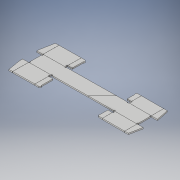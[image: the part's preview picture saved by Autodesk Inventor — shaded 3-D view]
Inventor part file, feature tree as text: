
AUTODESK INVENTOR PART (.ipt)
format: ipt  version: 2019 (Build 230136000, 136)  size: 731,648 bytes
history: native  units: mm
features: sheet_metal_op x10, sketch x4, projected_geometry x3, other x2
ambient origin geometry x8: Origin, YZ Plane, XZ Plane, XY Plane, X Axis, Y Axis, Z Axis, Center Point
bodies: Solid1 (feature_tree)
feature tree (19):
  sheet_metal_op  "Face1"
  sketch  "Sketch3"  dims[d13=5.0mm]
  sheet_metal_op  "Fold1"
  sheet_metal_op  "Fold2"
  sheet_metal_op  "Fold3"
  sheet_metal_op  "Fold4"
  sketch  "Sketch5"  dims[d14=9.0mm]
  sheet_metal_op  "Fold5"
  sheet_metal_op  "Fold6"
  sheet_metal_op  "Fold7"
  sheet_metal_op  "Fold8"
  sheet_metal_op  "Fold9"
  sketch  "Sketch2"  dims[d12=2.0mm]
  other  "Plate1"
  projected_geometry  "Projected Loop1"
  projected_geometry  "Projected Loop3"
  sketch  "Sketch6"  dims[d15=1.5mm d16=0.5mm d17=0.5mm d18=0.5mm d19=0.25mm d20=3.0mm d21=5.75mm d23=0.5mm d24=0.5mm d25=0.25mm d26=1.0mm d27=0.5mm d28=0.174533mm d29=0.5mm d30=0.5mm d31=0.25mm d32=1.0mm d33=0.5mm d34=0.174533mm d35=0.5mm d36=0.5mm d37=0.25mm d38=1.0mm d39=0.5mm d40=0.017453mm d41=0.5mm d42=0.5mm d43=0.25mm d44=1.0mm d45=0.5mm d46=0.017453mm d47=0.5mm d48=9.0mm d49=0.25mm d50=25.75mm d51=5.75mm d56=9.0mm d57=90.0deg d58=90.0deg d59=90.0deg d60=90.0deg d61=90.0deg d62=9.0mm d63=34.75mm d64=5.75mm d65=0.0mm d66=36.75mm d67=10.75mm d68=0.0mm d69=0.0mm d70=5.75mm d71=6.5mm d72=0.0mm d73=2.5mm d74=1.5mm d75=0.5mm d76=0.5mm d77=0.5mm d79=0.25mm d80=4.5mm d81=6.5mm d82=0.5mm d83=0.25mm d84=1.0mm d85=0.5mm d86=0.174533mm d87=0.5mm d88=0.5mm d89=0.25mm d90=1.0mm d91=0.5mm d92=0.174533mm d93=0.5mm d94=0.5mm d95=0.25mm d96=1.0mm d97=0.5mm d98=0.017453mm d99=0.5mm d100=0.5mm d101=0.25mm d102=1.0mm d103=0.5mm d104=0.017453mm d105=0.5mm d106=135.0deg d108=0.5mm d109=0.25mm d110=1.0mm d111=0.5mm d112=0.174533mm d113=0.5mm d115=0.5mm d116=1.973956mm d117=46.75mm d118=0.5mm d119=0.5mm d120=1.0mm d121=1.0mm d122=29.617392mm d123=29.617392mm d124=1.973956mm d125=46.756181mm]
  projected_geometry  "Projected Loop4"
  other  "Definition1"
